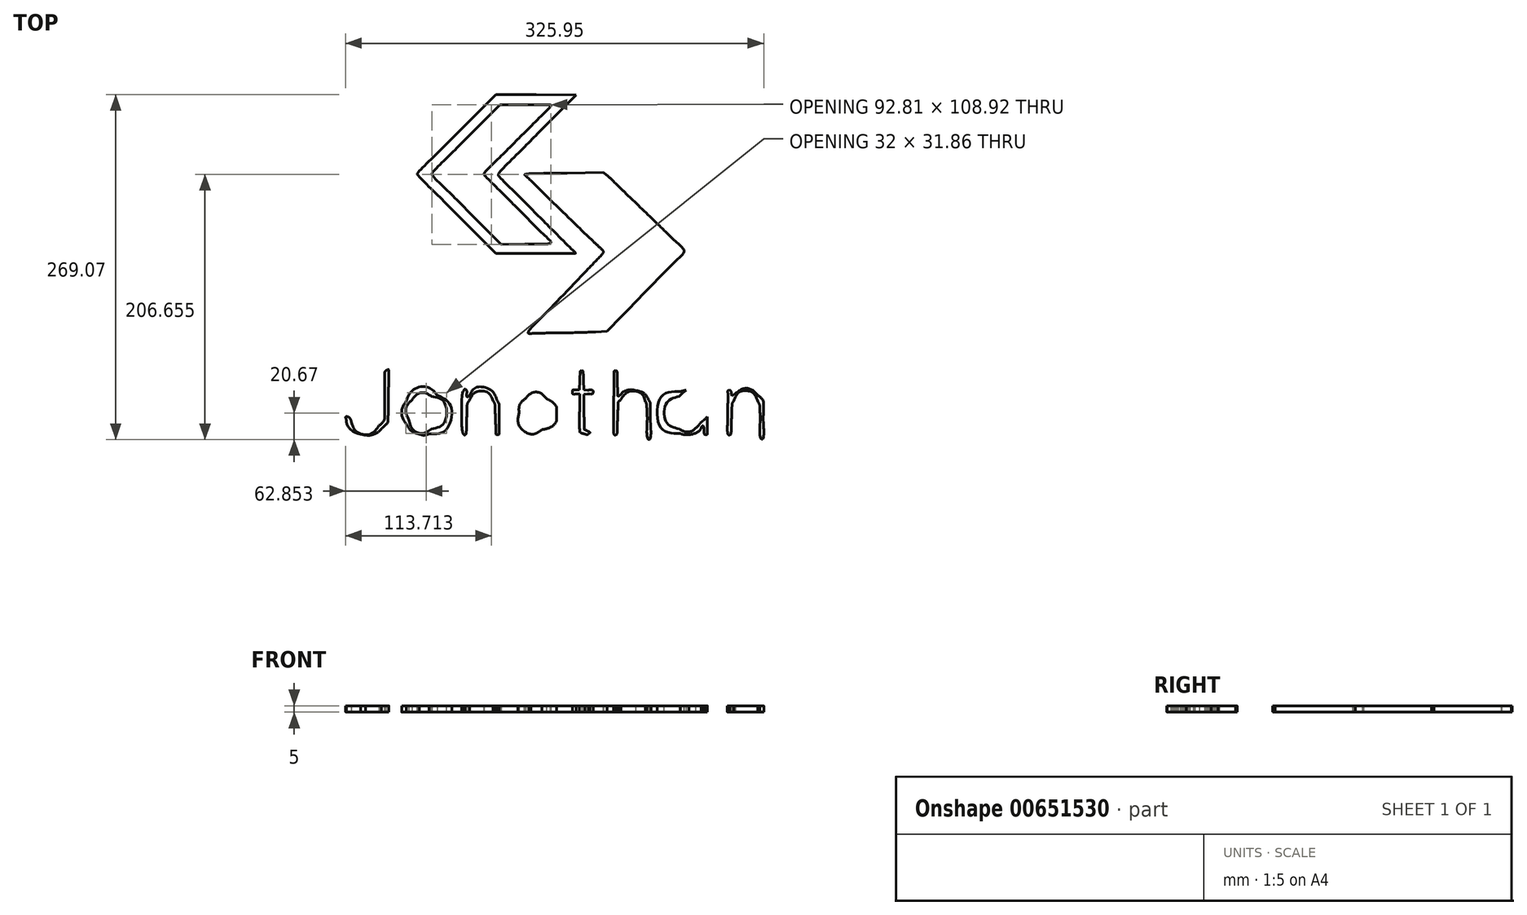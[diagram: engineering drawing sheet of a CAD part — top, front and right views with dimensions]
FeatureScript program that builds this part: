
annotation { "Feature Type Name" : "Feature", "Feature Type Description" : "" }
export const myFeature = defineFeature(function(context is Context, id is Id, definition is map)
    precondition{}
    {
        {
            var Q0;
            Q0=qCreatedBy(makeId("Top.planeOp"),FACE);
            var sketch = newSketch(context, id + "F0", { "sketchPlane" : qUnion([Q0])});
            skFitSpline(sketch, "E0", {"points": [v(-151.33, -132.02) * mm, v(-156.29, -130.54) * mm, v(-161.73, -125.25) * mm, v(-162.4, -121.27) * mm]});
            skFitSpline(sketch, "E1", {"points": [v(-162.4, -121.27) * mm, v(-162.86, -118.44) * mm, v(-160.33, -119.07) * mm, v(-158.65, -122.2) * mm]});
            skFitSpline(sketch, "E2", {"points": [v(-158.65, -122.2) * mm, v(-154.32, -130.3) * mm, v(-143.5, -131.85) * mm, v(-136.98, -125.33) * mm]});
            skFitSpline(sketch, "E3", {"points": [v(-136.98, -125.33) * mm, v(-133.2, -121.56) * mm, v(-132.66, -118.34) * mm, v(-132.66, -99.9) * mm]});
            skFitSpline(sketch, "E4", {"points": [v(-132.66, -99.9) * mm, v(-132.66, -88.61) * mm, v(-132.37, -83.16) * mm, v(-131.76, -82.79) * mm]});
            skFitSpline(sketch, "E5", {"points": [v(-131.76, -82.79) * mm, v(-129.79, -81.57) * mm, v(-129.4, -85.09) * mm, v(-129.66, -102.04) * mm]});
            skFitSpline(sketch, "E6", {"points": [v(-129.66, -102.04) * mm, v(-129.95, -121.5) * mm, v(-130.3, -123.19) * mm, v(-135.1, -127.86) * mm]});
            skFitSpline(sketch, "E7", {"points": [v(-135.1, -127.86) * mm, v(-137.72, -130.41) * mm, v(-144, -132.92) * mm, v(-147.4, -132.78) * mm]});
            skFitSpline(sketch, "E8", {"points": [v(-147.4, -132.78) * mm, v(-148.3, -132.74) * mm, v(-150.08, -132.4) * mm, v(-151.33, -132.02) * mm]});
            skFitSpline(sketch, "E9", {"points": [v(-105.64, -132.05) * mm, v(-109.78, -130.8) * mm, v(-113.47, -127.9) * mm, v(-115.66, -124.17) * mm]});
            skFitSpline(sketch, "E10", {"points": [v(-115.66, -124.17) * mm, v(-118.79, -118.85) * mm, v(-118.78, -111.62) * mm, v(-115.63, -106.27) * mm]});
            skFitSpline(sketch, "E11", {"points": [v(-115.63, -106.27) * mm, v(-110.53, -97.59) * mm, v(-99.23, -95.44) * mm, v(-91.62, -101.71) * mm]});
            skFitSpline(sketch, "E12", {"points": [v(-91.62, -101.71) * mm, v(-81.01, -110.46) * mm, v(-84.8, -128.67) * mm, v(-97.9, -131.97) * mm]});
            skFitSpline(sketch, "E13", {"points": [v(-97.9, -131.97) * mm, v(-101.83, -132.96) * mm, v(-102.58, -132.97) * mm, v(-105.64, -132.05) * mm]});
            skFitSpline(sketch, "E14", {"points": [v(-96.1, -127.97) * mm, v(-86.1, -123.13) * mm, v(-86.1, -107.35) * mm, v(-96.1, -102.52) * mm]});
            skFitSpline(sketch, "E15", {"points": [v(-96.1, -102.52) * mm, v(-101.77, -99.77) * mm, v(-106.88, -100.73) * mm, v(-111.2, -105.35) * mm]});
            skFitSpline(sketch, "E16", {"points": [v(-111.2, -105.35) * mm, v(-115.17, -109.59) * mm, v(-116.12, -115.15) * mm, v(-113.81, -120.66) * mm]});
            skFitSpline(sketch, "E17", {"points": [v(-113.81, -120.66) * mm, v(-110.48, -128.64) * mm, v(-103.46, -131.53) * mm, v(-96.1, -127.97) * mm]});
            skLineSegment(sketch, "E18", {"start": v(-105.64, -132.05) * mm, "end": v(-105.64, -132.05) * mm});
            skFitSpline(sketch, "E19", {"points": [v(-71.35, -131.61) * mm, v(-72.12, -129.61) * mm, v(-71.92, -99.79) * mm, v(-71.13, -98.54) * mm]});
            skFitSpline(sketch, "E20", {"points": [v(-71.13, -98.54) * mm, v(-70.15, -96.99) * mm, v(-68.65, -98.16) * mm, v(-68.65, -100.5) * mm]});
            skFitSpline(sketch, "E21", {"points": [v(-68.65, -100.5) * mm, v(-68.65, -102.86) * mm, v(-67.78, -102.97) * mm, v(-65.85, -100.84) * mm]});
            skFitSpline(sketch, "E22", {"points": [v(-65.85, -100.84) * mm, v(-61.02, -95.5) * mm, v(-49.48, -97.93) * mm, v(-45.35, -105.14) * mm]});
            skFitSpline(sketch, "E23", {"points": [v(-45.35, -105.14) * mm, v(-43.59, -108.21) * mm, v(-43.45, -109.29) * mm, v(-43.45, -120.44) * mm]});
            skFitSpline(sketch, "E24", {"points": [v(-43.45, -120.44) * mm, v(-43.45, -130.58) * mm, v(-43.64, -132.44) * mm, v(-44.65, -132.44) * mm]});
            skFitSpline(sketch, "E25", {"points": [v(-44.65, -132.44) * mm, v(-45.65, -132.44) * mm, v(-45.92, -130.4) * mm, v(-46.25, -120.4) * mm]});
            skFitSpline(sketch, "E26", {"points": [v(-46.25, -120.4) * mm, v(-46.57, -110.72) * mm, v(-46.93, -107.94) * mm, v(-48.06, -106.22) * mm]});
            skFitSpline(sketch, "E27", {"points": [v(-48.06, -106.22) * mm, v(-52.45, -99.54) * mm, v(-61.8, -99.38) * mm, v(-66.6, -105.9) * mm]});
            skFitSpline(sketch, "E28", {"points": [v(-66.6, -105.9) * mm, v(-68.05, -107.88) * mm, v(-68.3, -109.65) * mm, v(-68.65, -120.24) * mm]});
            skFitSpline(sketch, "E29", {"points": [v(-68.65, -120.24) * mm, v(-68.92, -128.16) * mm, v(-69.36, -132.42) * mm, v(-69.95, -132.61) * mm]});
            skFitSpline(sketch, "E30", {"points": [v(-69.95, -132.61) * mm, v(-70.45, -132.78) * mm, v(-71.08, -132.33) * mm, v(-71.35, -131.61) * mm]});
            skFitSpline(sketch, "E31", {"points": [v(-19.38, -131.85) * mm, v(-23.44, -130.78) * mm, v(-29.06, -125.2) * mm, v(-30.19, -121.12) * mm]});
            skFitSpline(sketch, "E32", {"points": [v(-30.19, -121.12) * mm, v(-32.16, -114.04) * mm, v(-30.61, -107.57) * mm, v(-25.8, -102.76) * mm]});
            skFitSpline(sketch, "E33", {"points": [v(-25.8, -102.76) * mm, v(-19.85, -96.8) * mm, v(-11.24, -96.37) * mm, v(-4.5, -101.7) * mm]});
            skFitSpline(sketch, "E34", {"points": [v(-1.3, -101.04) * mm, v(-1.13, -99.02) * mm, v(-0.66, -98.04) * mm, v(0.15, -98.04) * mm]});
            skFitSpline(sketch, "E35", {"points": [v(0.15, -98.04) * mm, v(1.18, -98.04) * mm, v(1.35, -100.49) * mm, v(1.35, -115.24) * mm]});
            skFitSpline(sketch, "E36", {"points": [v(1.35, -115.24) * mm, v(1.35, -130) * mm, v(1.18, -132.44) * mm, v(0.15, -132.44) * mm]});
            skFitSpline(sketch, "E37", {"points": [v(0.15, -132.44) * mm, v(-0.66, -132.44) * mm, v(-1.13, -131.47) * mm, v(-1.3, -129.44) * mm]});
            skLineSegment(sketch, "E38", {"start": v(-4.5, -101.7) * mm, "end": v(-1.55, -104.04) * mm});
            skLineSegment(sketch, "E39", {"start": v(-1.55, -104.04) * mm, "end": v(-1.3, -101.04) * mm});
            skFitSpline(sketch, "E40", {"points": [v(-4.3, -128.53) * mm, v(-7.32, -130.84) * mm, v(-12.16, -132.8) * mm, v(-14.65, -132.73) * mm]});
            skFitSpline(sketch, "E41", {"points": [v(-14.65, -132.73) * mm, v(-15.53, -132.7) * mm, v(-17.66, -132.3) * mm, v(-19.38, -131.85) * mm]});
            skLineSegment(sketch, "E42", {"start": v(-1.3, -129.44) * mm, "end": v(-1.55, -126.44) * mm});
            skLineSegment(sketch, "E43", {"start": v(-1.55, -126.44) * mm, "end": v(-4.3, -128.53) * mm});
            skFitSpline(sketch, "E44", {"points": [v(-10.03, -128.54) * mm, v(-0.3, -124.38) * mm, v(1.58, -111.38) * mm, v(-6.52, -104.27) * mm]});
            skFitSpline(sketch, "E45", {"points": [v(-6.52, -104.27) * mm, v(-11.58, -99.83) * mm, v(-17.75, -99.84) * mm, v(-22.83, -104.3) * mm]});
            skFitSpline(sketch, "E46", {"points": [v(-22.83, -104.3) * mm, v(-26.33, -107.38) * mm, v(-27.85, -110.83) * mm, v(-27.85, -115.66) * mm]});
            skFitSpline(sketch, "E47", {"points": [v(-27.85, -115.66) * mm, v(-27.85, -125.23) * mm, v(-18.35, -132.1) * mm, v(-10.03, -128.54) * mm]});
            skFitSpline(sketch, "E48", {"points": [v(23.26, -131.9) * mm, v(19.88, -130.74) * mm, v(19.35, -128.28) * mm, v(19.35, -114) * mm]});
            skLineSegment(sketch, "E49", {"start": v(-10.03, -128.54) * mm, "end": v(-10.03, -128.54) * mm});
            skFitSpline(sketch, "E50", {"points": [v(16.55, -100.84) * mm, v(14.28, -100.84) * mm, v(13.75, -100.54) * mm, v(13.75, -99.24) * mm]});
            skFitSpline(sketch, "E51", {"points": [v(13.75, -99.24) * mm, v(13.75, -97.95) * mm, v(14.28, -97.64) * mm, v(16.52, -97.64) * mm]});
            skLineSegment(sketch, "E52", {"start": v(19.35, -114) * mm, "end": v(19.35, -100.84) * mm});
            skLineSegment(sketch, "E53", {"start": v(19.35, -100.84) * mm, "end": v(16.55, -100.84) * mm});
            skFitSpline(sketch, "E54", {"points": [v(19.52, -90.24) * mm, v(19.7, -84.3) * mm, v(19.98, -82.84) * mm, v(20.95, -82.84) * mm]});
            skFitSpline(sketch, "E55", {"points": [v(20.95, -82.84) * mm, v(21.91, -82.84) * mm, v(22.2, -84.3) * mm, v(22.38, -90.2) * mm]});
            skLineSegment(sketch, "E56", {"start": v(16.52, -97.64) * mm, "end": v(19.29, -97.64) * mm});
            skLineSegment(sketch, "E57", {"start": v(19.29, -97.64) * mm, "end": v(19.52, -90.24) * mm});
            skFitSpline(sketch, "E58", {"points": [v(25.58, -97.8) * mm, v(29.7, -98.14) * mm, v(29.66, -100.35) * mm, v(25.53, -100.7) * mm]});
            skLineSegment(sketch, "E59", {"start": v(22.38, -90.2) * mm, "end": v(22.6, -97.55) * mm});
            skLineSegment(sketch, "E60", {"start": v(22.6, -97.55) * mm, "end": v(25.58, -97.8) * mm});
            skFitSpline(sketch, "E61", {"points": [v(22.73, -114.67) * mm, v(22.94, -128.04) * mm, v(23, -128.42) * mm, v(24.76, -129.3) * mm]});
            skFitSpline(sketch, "E62", {"points": [v(24.76, -129.3) * mm, v(27.31, -130.57) * mm, v(27.52, -130.9) * mm, v(26.37, -131.82) * mm]});
            skFitSpline(sketch, "E63", {"points": [v(26.37, -131.82) * mm, v(25.73, -132.33) * mm, v(24.57, -132.36) * mm, v(23.26, -131.9) * mm]});
            skLineSegment(sketch, "E64", {"start": v(25.53, -100.7) * mm, "end": v(22.5, -100.94) * mm});
            skLineSegment(sketch, "E65", {"start": v(22.5, -100.94) * mm, "end": v(22.73, -114.67) * mm});
            skFitSpline(sketch, "E66", {"points": [v(46.14, -131.9) * mm, v(45.9, -131.31) * mm, v(45.82, -120.03) * mm, v(45.94, -106.84) * mm]});
            skFitSpline(sketch, "E67", {"points": [v(45.94, -106.84) * mm, v(46.12, -86.14) * mm, v(46.31, -82.84) * mm, v(47.35, -82.84) * mm]});
            skFitSpline(sketch, "E68", {"points": [v(47.35, -82.84) * mm, v(48.34, -82.84) * mm, v(48.59, -84.57) * mm, v(48.77, -92.64) * mm]});
            skFitSpline(sketch, "E69", {"points": [v(48.77, -92.64) * mm, v(48.9, -98.03) * mm, v(49.23, -102.44) * mm, v(49.52, -102.44) * mm]});
            skFitSpline(sketch, "E70", {"points": [v(49.52, -102.44) * mm, v(49.8, -102.44) * mm, v(50.84, -101.7) * mm, v(51.82, -100.78) * mm]});
            skFitSpline(sketch, "E71", {"points": [v(51.82, -100.78) * mm, v(53.99, -98.74) * mm, v(59.55, -97.4) * mm, v(62.88, -98.1) * mm]});
            skFitSpline(sketch, "E72", {"points": [v(62.88, -98.1) * mm, v(67.09, -98.99) * mm, v(71.08, -101.7) * mm, v(72.87, -104.89) * mm]});
            skFitSpline(sketch, "E73", {"points": [v(72.87, -104.89) * mm, v(74.45, -107.69) * mm, v(74.57, -108.92) * mm, v(74.37, -120) * mm]});
            skFitSpline(sketch, "E74", {"points": [v(74.37, -120) * mm, v(74.08, -135.84) * mm, v(72.7, -136) * mm, v(72.11, -120.25) * mm]});
            skFitSpline(sketch, "E75", {"points": [v(72.11, -120.25) * mm, v(71.86, -113.42) * mm, v(71.27, -107.71) * mm, v(70.72, -106.7) * mm]});
            skFitSpline(sketch, "E76", {"points": [v(70.72, -106.7) * mm, v(67.06, -100.08) * mm, v(57.2, -99.15) * mm, v(51.68, -104.91) * mm]});
            skFitSpline(sketch, "E77", {"points": [v(51.68, -104.91) * mm, v(49.35, -107.34) * mm, v(49.35, -107.36) * mm, v(48.95, -119.83) * mm]});
            skFitSpline(sketch, "E78", {"points": [v(48.95, -119.83) * mm, v(48.66, -128.81) * mm, v(48.27, -132.4) * mm, v(47.55, -132.65) * mm]});
            skFitSpline(sketch, "E79", {"points": [v(47.55, -132.65) * mm, v(47, -132.83) * mm, v(46.36, -132.5) * mm, v(46.14, -131.9) * mm]});
            skLineSegment(sketch, "E80", {"start": v(23.26, -131.9) * mm, "end": v(23.26, -131.9) * mm});
            skFitSpline(sketch, "E81", {"points": [v(97.85, -131.68) * mm, v(82.5, -126.74) * mm, v(82.86, -103.25) * mm, v(98.35, -98.75) * mm]});
            skFitSpline(sketch, "E82", {"points": [v(98.35, -98.75) * mm, v(100.88, -98.01) * mm, v(103.6, -97.74) * mm, v(105.16, -98.06) * mm]});
            skFitSpline(sketch, "E83", {"points": [v(105.16, -98.06) * mm, v(108.26, -98.7) * mm, v(114.55, -102.2) * mm, v(114.55, -103.28) * mm]});
            skFitSpline(sketch, "E84", {"points": [v(114.55, -103.28) * mm, v(114.55, -103.7) * mm, v(114.89, -104.04) * mm, v(115.3, -104.04) * mm]});
            skFitSpline(sketch, "E85", {"points": [v(115.3, -104.04) * mm, v(115.71, -104.04) * mm, v(116.16, -102.7) * mm, v(116.3, -101.04) * mm]});
            skFitSpline(sketch, "E86", {"points": [v(116.3, -101.04) * mm, v(116.47, -99.02) * mm, v(116.94, -98.04) * mm, v(117.75, -98.04) * mm]});
            skFitSpline(sketch, "E87", {"points": [v(117.75, -98.04) * mm, v(118.78, -98.04) * mm, v(118.95, -100.49) * mm, v(118.95, -115.24) * mm]});
            skFitSpline(sketch, "E88", {"points": [v(118.95, -115.24) * mm, v(118.95, -130) * mm, v(118.78, -132.44) * mm, v(117.75, -132.44) * mm]});
            skFitSpline(sketch, "E89", {"points": [v(117.75, -132.44) * mm, v(116.94, -132.44) * mm, v(116.47, -131.47) * mm, v(116.3, -129.44) * mm]});
            skFitSpline(sketch, "E90", {"points": [v(116.3, -129.44) * mm, v(116.04, -126.36) * mm, v(115.11, -125.6) * mm, v(113.99, -127.56) * mm]});
            skFitSpline(sketch, "E91", {"points": [v(113.99, -127.56) * mm, v(112.94, -129.4) * mm, v(107.97, -131.93) * mm, v(104.55, -132.39) * mm]});
            skFitSpline(sketch, "E92", {"points": [v(104.55, -132.39) * mm, v(102.77, -132.62) * mm, v(99.8, -132.3) * mm, v(97.85, -131.68) * mm]});
            skFitSpline(sketch, "E93", {"points": [v(109.64, -127.46) * mm, v(110.8, -126.6) * mm, v(112.55, -124.72) * mm, v(113.53, -123.28) * mm]});
            skFitSpline(sketch, "E94", {"points": [v(113.53, -123.28) * mm, v(121.54, -111.5) * mm, v(109.18, -96.12) * mm, v(96.95, -102.64) * mm]});
            skFitSpline(sketch, "E95", {"points": [v(96.95, -102.64) * mm, v(87.05, -107.92) * mm, v(87.15, -122.93) * mm, v(97.13, -128) * mm]});
            skFitSpline(sketch, "E96", {"points": [v(97.13, -128) * mm, v(101.21, -130.07) * mm, v(106.41, -129.85) * mm, v(109.64, -127.46) * mm]});
            skFitSpline(sketch, "E97", {"points": [v(134.93, -131.89) * mm, v(134.7, -131.3) * mm, v(134.61, -123.43) * mm, v(134.73, -114.42) * mm]});
            skFitSpline(sketch, "E98", {"points": [v(134.73, -114.42) * mm, v(134.91, -100.5) * mm, v(135.13, -98.04) * mm, v(136.15, -98.04) * mm]});
            skFitSpline(sketch, "E99", {"points": [v(136.15, -98.04) * mm, v(136.86, -98.04) * mm, v(137.45, -98.93) * mm, v(137.6, -100.22) * mm]});
            skFitSpline(sketch, "E100", {"points": [v(140.8, -100.5) * mm, v(146.63, -96.73) * mm, v(152.94, -97.18) * mm, v(158.15, -101.75) * mm]});
            skFitSpline(sketch, "E101", {"points": [v(158.15, -101.75) * mm, v(161.99, -105.12) * mm, v(162.68, -108.26) * mm, v(162.4, -121.05) * mm]});
            skFitSpline(sketch, "E102", {"points": [v(162.4, -121.05) * mm, v(162.06, -135.79) * mm, v(160.67, -135.54) * mm, v(160.15, -120.65) * mm]});
            skFitSpline(sketch, "E103", {"points": [v(160.15, -120.65) * mm, v(159.81, -111.15) * mm, v(159.48, -108.8) * mm, v(158.15, -106.53) * mm]});
            skFitSpline(sketch, "E104", {"points": [v(158.15, -106.53) * mm, v(153.95, -99.43) * mm, v(144.13, -99.26) * mm, v(139.56, -106.22) * mm]});
            skFitSpline(sketch, "E105", {"points": [v(139.56, -106.22) * mm, v(138.42, -107.94) * mm, v(138.07, -110.72) * mm, v(137.75, -120.34) * mm]});
            skFitSpline(sketch, "E106", {"points": [v(137.75, -120.34) * mm, v(137.46, -128.91) * mm, v(137.06, -132.4) * mm, v(136.35, -132.65) * mm]});
            skFitSpline(sketch, "E107", {"points": [v(136.35, -132.65) * mm, v(135.8, -132.83) * mm, v(135.16, -132.49) * mm, v(134.93, -131.89) * mm]});
            skLineSegment(sketch, "E108", {"start": v(137.6, -100.22) * mm, "end": v(137.85, -102.4) * mm});
            skLineSegment(sketch, "E109", {"start": v(137.85, -102.4) * mm, "end": v(140.8, -100.5) * mm});
            skFitSpline(sketch, "E110", {"points": [v(-20.5, -52.5) * mm, v(-20.27, -51.45) * mm, v(-11.72, -42.4) * mm, v(23.55, -5.8) * mm]});
            skFitSpline(sketch, "E111", {"points": [v(23.55, -5.8) * mm, v(31.36, 2.3) * mm, v(37.75, 9.37) * mm, v(37.75, 9.92) * mm]});
            skFitSpline(sketch, "E112", {"points": [v(37.75, 9.92) * mm, v(37.75, 10.46) * mm, v(34.6, 13.89) * mm, v(30.75, 17.54) * mm]});
            skFitSpline(sketch, "E113", {"points": [v(30.75, 17.54) * mm, v(24.02, 23.92) * mm, v(14.43, 33.21) * mm, v(-11.54, 58.54) * mm]});
            skFitSpline(sketch, "E114", {"points": [v(-11.54, 58.54) * mm, v(-23.5, 70.21) * mm, v(-23.6, 70.33) * mm, v(-21.14, 70.7) * mm]});
            skFitSpline(sketch, "E115", {"points": [v(-21.14, 70.7) * mm, v(-19.77, 70.9) * mm, v(-5.92, 71.27) * mm, v(9.64, 71.5) * mm]});
            skFitSpline(sketch, "E116", {"points": [v(40.44, 69.86) * mm, v(41.82, 68.71) * mm, v(47.81, 63.04) * mm, v(53.76, 57.26) * mm]});
            skFitSpline(sketch, "E117", {"points": [v(53.76, 57.26) * mm, v(59.71, 51.48) * mm, v(72.77, 38.85) * mm, v(82.79, 29.18) * mm]});
            skFitSpline(sketch, "E118", {"points": [v(82.79, 29.18) * mm, v(92.8, 19.51) * mm, v(100.9, 11.16) * mm, v(100.77, 10.62) * mm]});
            skFitSpline(sketch, "E119", {"points": [v(100.77, 10.62) * mm, v(100.5, 9.44) * mm, v(93.85, 2.47) * mm, v(52.33, -40.17) * mm]});
            skLineSegment(sketch, "E120", {"start": v(9.64, 71.5) * mm, "end": v(37.93, 71.95) * mm});
            skLineSegment(sketch, "E121", {"start": v(37.93, 71.95) * mm, "end": v(40.44, 69.86) * mm});
            skFitSpline(sketch, "E122", {"points": [v(31.93, -52.34) * mm, v(26.99, -52.6) * mm, v(13.11, -52.98) * mm, v(1.1, -53.2) * mm]});
            skFitSpline(sketch, "E123", {"points": [v(1.1, -53.2) * mm, v(-17.35, -53.55) * mm, v(-20.72, -53.44) * mm, v(-20.5, -52.5) * mm]});
            skLineSegment(sketch, "E124", {"start": v(52.33, -40.17) * mm, "end": v(40.92, -51.89) * mm});
            skLineSegment(sketch, "E125", {"start": v(40.92, -51.89) * mm, "end": v(31.93, -52.34) * mm});
            skFitSpline(sketch, "E126", {"points": [v(-76.46, 39.36) * mm, v(-93.28, 56.2) * mm, v(-107.05, 70.32) * mm, v(-107.05, 70.76) * mm]});
            skFitSpline(sketch, "E127", {"points": [v(-107.05, 70.76) * mm, v(-107.05, 71.2) * mm, v(-93.28, 85.34) * mm, v(-76.44, 102.17) * mm]});
            skFitSpline(sketch, "E128", {"points": [v(-13.45, 102.14) * mm, v(-29.95, 85.52) * mm, v(-43.58, 71.35) * mm, v(-43.73, 70.65) * mm]});
            skFitSpline(sketch, "E129", {"points": [v(-43.73, 70.65) * mm, v(-43.9, 69.84) * mm, v(-33.03, 58.38) * mm, v(-14.13, 39.44) * mm]});
            skFitSpline(sketch, "E130", {"points": [v(-14.13, 39.44) * mm, v(2.3, 22.97) * mm, v(15.9, 9.33) * mm, v(16.08, 9.13) * mm]});
            skFitSpline(sketch, "E131", {"points": [v(16.08, 9.13) * mm, v(16.26, 8.92) * mm, v(2.4, 8.76) * mm, v(-14.72, 8.76) * mm]});
            skLineSegment(sketch, "E132", {"start": v(-76.44, 102.17) * mm, "end": v(-45.83, 132.78) * mm});
            skLineSegment(sketch, "E133", {"start": v(-45.83, 132.78) * mm, "end": v(-14.64, 132.57) * mm});
            skLineSegment(sketch, "E134", {"start": v(-14.64, 132.57) * mm, "end": v(16.55, 132.36) * mm});
            skLineSegment(sketch, "E135", {"start": v(16.55, 132.36) * mm, "end": v(-13.45, 102.14) * mm});
            skFitSpline(sketch, "E136", {"points": [v(-3.77, 16.82) * mm, v(-2.93, 17.34) * mm, v(-9.14, 24) * mm, v(-28.85, 43.74) * mm]});
            skFitSpline(sketch, "E137", {"points": [v(-28.85, 43.74) * mm, v(-43.26, 58.16) * mm, v(-55.05, 70.33) * mm, v(-55.05, 70.77) * mm]});
            skFitSpline(sketch, "E138", {"points": [v(-55.05, 70.77) * mm, v(-55.05, 71.2) * mm, v(-43.35, 83.26) * mm, v(-29.05, 97.56) * mm]});
            skFitSpline(sketch, "E139", {"points": [v(-29.05, 97.56) * mm, v(-14.75, 111.85) * mm, v(-3.05, 123.82) * mm, v(-3.05, 124.15) * mm]});
            skFitSpline(sketch, "E140", {"points": [v(-3.05, 124.15) * mm, v(-3.05, 124.48) * mm, v(-11.97, 124.76) * mm, v(-22.87, 124.76) * mm]});
            skLineSegment(sketch, "E141", {"start": v(-14.72, 8.76) * mm, "end": v(-45.86, 8.76) * mm});
            skLineSegment(sketch, "E142", {"start": v(-45.86, 8.76) * mm, "end": v(-76.46, 39.36) * mm});
            skFitSpline(sketch, "E143", {"points": [v(-69.06, 98.39) * mm, v(-83.56, 83.89) * mm, v(-95.57, 71.6) * mm, v(-95.74, 71.1) * mm]});
            skFitSpline(sketch, "E144", {"points": [v(-95.74, 71.1) * mm, v(-95.91, 70.58) * mm, v(-83.86, 57.96) * mm, v(-68.95, 43.03) * mm]});
            skLineSegment(sketch, "E145", {"start": v(-22.87, 124.76) * mm, "end": v(-42.68, 124.76) * mm});
            skLineSegment(sketch, "E146", {"start": v(-42.68, 124.76) * mm, "end": v(-69.06, 98.39) * mm});
            skFitSpline(sketch, "E147", {"points": [v(-23.37, 16.01) * mm, v(-13.2, 16.07) * mm, v(-4.39, 16.43) * mm, v(-3.77, 16.82) * mm]});
            skLineSegment(sketch, "E148", {"start": v(-68.95, 43.03) * mm, "end": v(-41.85, 15.9) * mm});
            skLineSegment(sketch, "E149", {"start": v(-41.85, 15.9) * mm, "end": v(-23.37, 16.01) * mm});
            skSolve(sketch);
        }
        {
            var Q0;
            Q0=makeQuery(id+"F0.imprint","IMPRINT",FACE,{"disambiguationData":[TD([[makeQuery(id+"F0.imprint","IMPRINT",EDGE,{"derivedFrom":sQuery(id+"F0.wireOp",EDGE,"E126")}),-1.0]])]});
            var Q1;
            Q1=makeQuery(id+"F0.imprint","IMPRINT",FACE,{"disambiguationData":[TD([[makeQuery(id+"F0.imprint","IMPRINT",EDGE,{"derivedFrom":sQuery(id+"F0.wireOp",EDGE,"E110")}),-1.0]])]});
            var Q2;
            Q2=makeQuery(id+"F0.imprint","IMPRINT",FACE,{"disambiguationData":[TD([[makeQuery(id+"F0.imprint","IMPRINT",EDGE,{"derivedFrom":sQuery(id+"F0.wireOp",EDGE,"E0")}),-1.0]])]});
            var Q3;
            Q3=makeQuery(id+"F0.imprint","IMPRINT",FACE,{"disambiguationData":[TD([[makeQuery(id+"F0.imprint","IMPRINT",EDGE,{"derivedFrom":sQuery(id+"F0.wireOp",EDGE,"E9")}),-1.0]])]});
            var Q4;
            Q4=makeQuery(id+"F0.imprint","IMPRINT",FACE,{"disambiguationData":[TD([[makeQuery(id+"F0.imprint","IMPRINT",EDGE,{"derivedFrom":sQuery(id+"F0.wireOp",EDGE,"E19")}),-1.0]])]});
            var Q5;
            Q5=makeQuery(id+"F0.imprint","IMPRINT",FACE,{"disambiguationData":[TD([[makeQuery(id+"F0.imprint","IMPRINT",EDGE,{"derivedFrom":sQuery(id+"F0.wireOp",EDGE,"E31")}),-1.0]])]});
            var Q6;
            Q6=makeQuery(id+"F0.imprint","IMPRINT",FACE,{"disambiguationData":[TD([[makeQuery(id+"F0.imprint","IMPRINT",EDGE,{"derivedFrom":sQuery(id+"F0.wireOp",EDGE,"E48")}),-1.0]])]});
            var Q7;
            Q7=makeQuery(id+"F0.imprint","IMPRINT",FACE,{"disambiguationData":[TD([[makeQuery(id+"F0.imprint","IMPRINT",EDGE,{"derivedFrom":sQuery(id+"F0.wireOp",EDGE,"E66")}),-1.0]])]});
            var Q8;
            Q8=makeQuery(id+"F0.imprint","IMPRINT",FACE,{"disambiguationData":[TD([[makeQuery(id+"F0.imprint","IMPRINT",EDGE,{"derivedFrom":sQuery(id+"F0.wireOp",EDGE,"E81")}),-1.0]])]});
            var Q9;
            Q9=makeQuery(id+"F0.imprint","IMPRINT",FACE,{"disambiguationData":[TD([[makeQuery(id+"F0.imprint","IMPRINT",EDGE,{"derivedFrom":sQuery(id+"F0.wireOp",EDGE,"E97")}),-1.0]])]});
            extrude(context, id + "F1", {"entities" : qUnion([Q0, Q1, Q2, Q3, Q4, Q5, Q6, Q7, Q8, Q9]), "depth" : 5 * mm, "offsetDistance" : 25 * mm});
        }
    });
